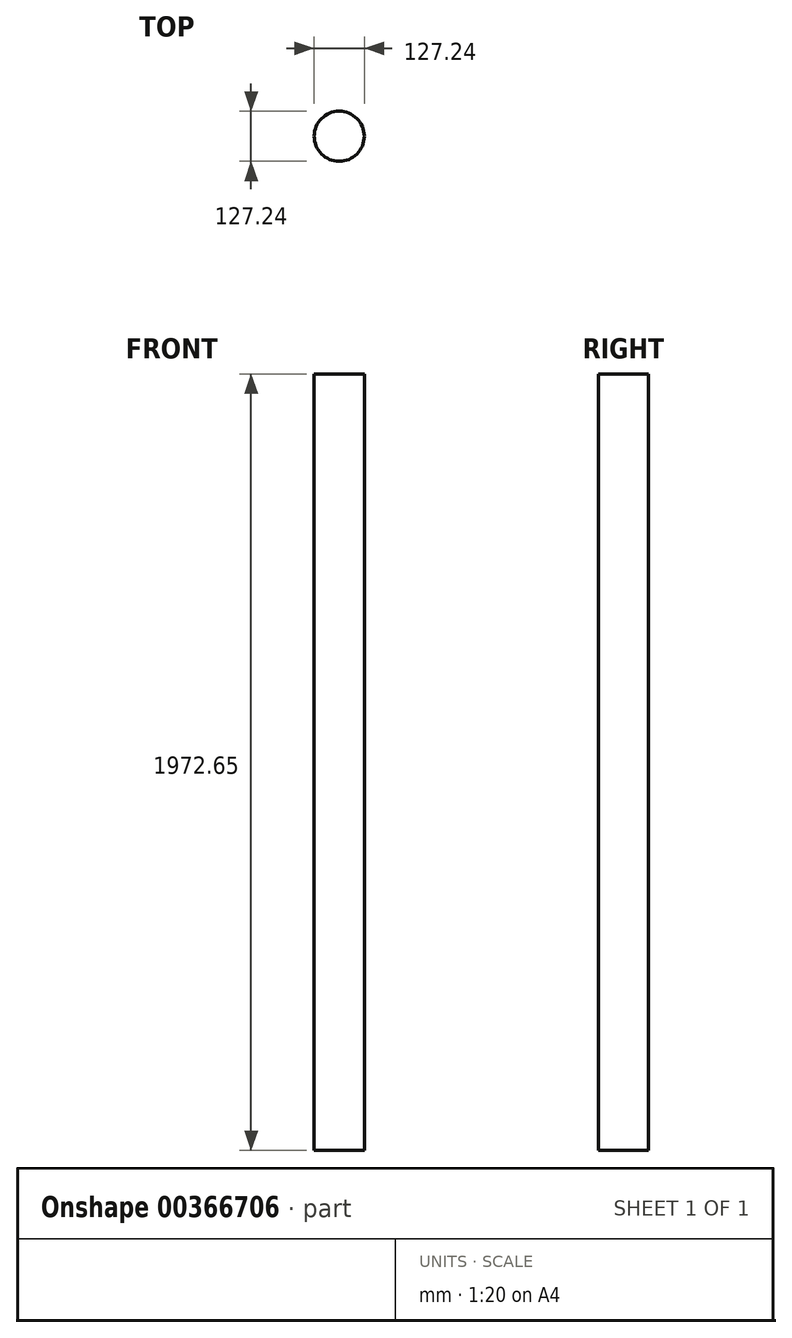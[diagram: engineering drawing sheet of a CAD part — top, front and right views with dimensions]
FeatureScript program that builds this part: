
annotation { "Feature Type Name" : "Feature", "Feature Type Description" : "" }
export const myFeature = defineFeature(function(context is Context, id is Id, definition is map)
    precondition{}
    {
        {
            var Q0;
            Q0=qCreatedBy(makeId("Top.planeOp"),FACE);
            var sketch = newSketch(context, id + "F0", { "sketchPlane" : qUnion([Q0])});
            skCircle(sketch, "E0", {"center": v(0, 0) * mm, "radius": 63.62 * mm});
            skSolve(sketch);
        }
        {
            var Q0;
            Q0=makeQuery(id+"F0.imprint","IMPRINT",FACE,{"disambiguationData":[TD([[makeQuery(id+"F0.imprint","IMPRINT",EDGE,{"derivedFrom":sQuery(id+"F0.wireOp",EDGE,"E0")}),1.0]])]});
            extrude(context, id + "F1", {"entities" : qUnion([Q0]), "depth" : 1500 * mm});
        }
        {
            var Q0;
            Q0=makeQuery(id+"F1.opExtrude","CAP_FACE",FACE,{"disambiguationData":[OSD([sQuery(id+"F0.wireOp",EDGE,"E0")])],"isStart":false});
            var sketch = newSketch(context, id + "F2", { "sketchPlane" : qUnion([Q0])});
            skSolve(sketch);
        }
        {
            var Q0;
            Q0=makeQuery(id+"F2.imprint","IMPRINT",FACE,{"disambiguationData":[TD([[makeQuery(id+"F2.imprint","IMPRINT",EDGE,{"derivedFrom":makeQuery(id+"F1.opExtrude","CAP_EDGE",EDGE,{"disambiguationData":[OSD([sQuery(id+"F0.wireOp",EDGE,"E0")])],"isStart":false})}),1.0]])]});
            extrude(context, id + "F3", {"entities" : qUnion([Q0]), "operationType" : NewBodyOperationType.ADD, "oppositeDirection" : true, "depth" : 1972.65 * mm});
        }
    });
